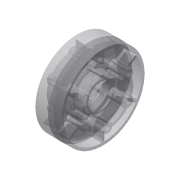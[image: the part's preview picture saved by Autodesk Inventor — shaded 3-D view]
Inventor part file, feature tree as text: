
AUTODESK INVENTOR PART (.ipt)
format: ipt  version: 2013 (Build 170138000, 138)  size: 1,170,944 bytes
history: native  units: in
note: dims shown in document units (in); Inventor stores cm internally (conversion verified against a paired STEP export)
features: fillet x2, imported_body x2, other x1
ambient origin geometry x8: Origin, YZ Plane, XZ Plane, XY Plane, X Axis, Y Axis, Z Axis, Center Point
feature tree (5):
  fillet  "Fillet10"  [1 undecoded]
  other  "4in 2013 Hub1"
  fillet  "Fillet9"  [1 undecoded]
  imported_body  "Base1"
  imported_body  "Base2"
note: 2 required parameter values undecoded (feature->parameter linkage not recoverable at this tier; creation-order binding heuristic only, values carry confidence <= 0.55)
